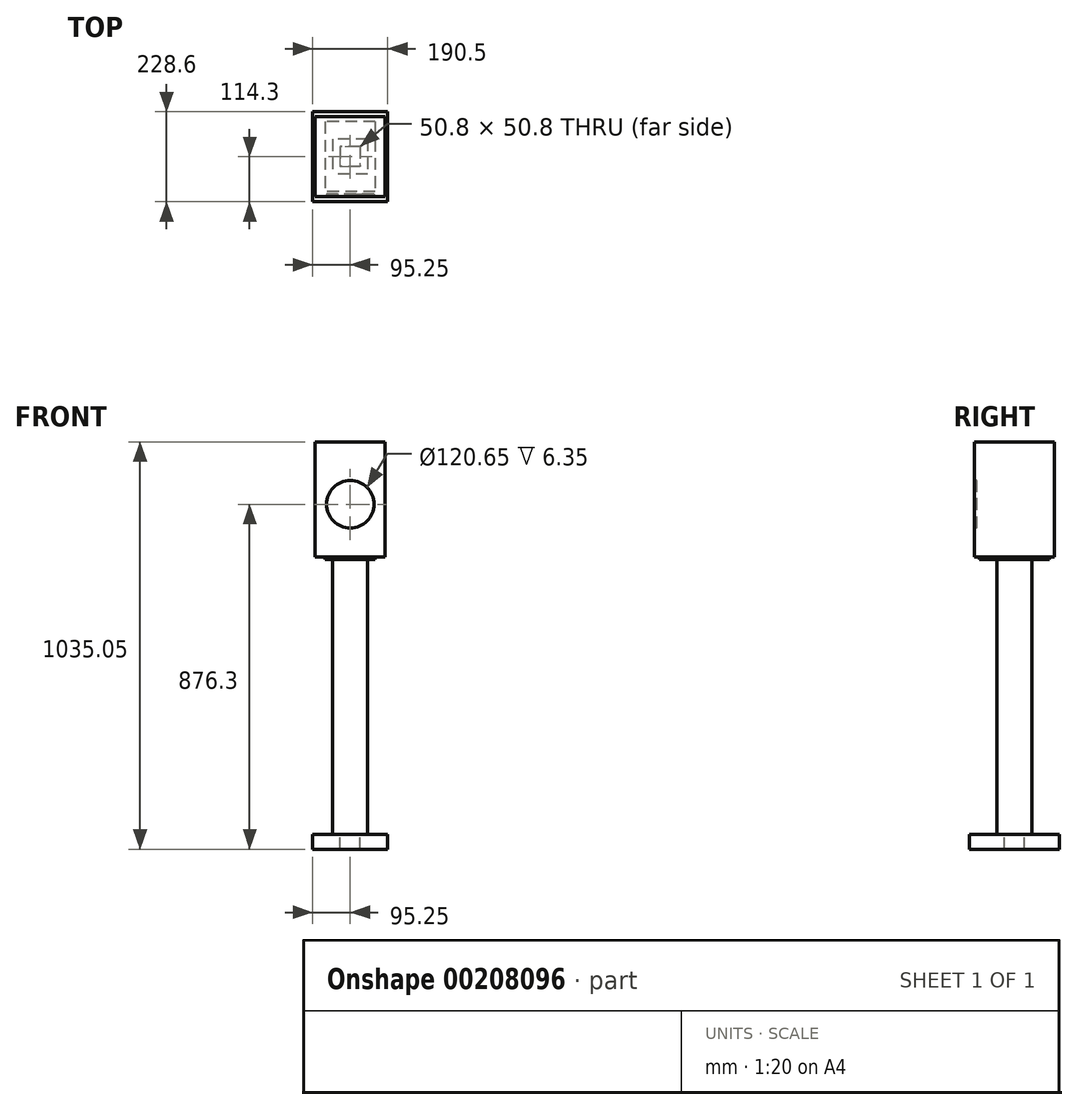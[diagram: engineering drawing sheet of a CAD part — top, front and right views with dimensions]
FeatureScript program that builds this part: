
annotation { "Feature Type Name" : "Feature", "Feature Type Description" : "" }
export const myFeature = defineFeature(function(context is Context, id is Id, definition is map)
    precondition{}
    {
        {
            var Q0;
            Q0=qCreatedBy(makeId("Top.planeOp"),FACE);
            var sketch = newSketch(context, id + "F0", { "sketchPlane" : qUnion([Q0])});
            skLineSegment(sketch, "E0.bottom", {"start": v(88.9, -101.6) * mm, "end": v(-88.9, -101.6) * mm});
            skLineSegment(sketch, "E0.top", {"start": v(88.9, 101.6) * mm, "end": v(-88.9, 101.6) * mm});
            skLineSegment(sketch, "E0.left", {"start": v(88.9, -101.6) * mm, "end": v(88.9, 101.6) * mm});
            skLineSegment(sketch, "E0.right", {"start": v(-88.9, -101.6) * mm, "end": v(-88.9, 101.6) * mm});
            skPoint(sketch, "E0.middle", {"position": v(0, 0) * mm});
            skSolve(sketch);
        }
        {
            var Q0;
            Q0 = qSketchRegion(id + "F0", true);
            extrude(context, id + "F1", {"entities" : qUnion([Q0]), "depth" : 292.1 * mm});
        }
        {
            var Q0;
            Q0=makeQuery(id+"F1.opExtrude","SWEPT_FACE",FACE,{"disambiguationData":[OSD([sQuery(id+"F0.wireOp",EDGE,"E0.bottom")])]});
            var sketch = newSketch(context, id + "F6", { "sketchPlane" : qUnion([Q0])});
            skLineSegment(sketch, "E1", {"start": v(0, 292.1) * mm, "end": v(0, 0) * mm, "construction": true});
            skCircle(sketch, "E2", {"center": v(0, 133.35) * mm, "radius": 60.33 * mm});
            skSolve(sketch);
        }
        {
            var Q0;
            Q0 = qSketchRegion(id + "F6", true);
            extrude(context, id + "F2", {"entities" : qUnion([Q0]), "operationType" : NewBodyOperationType.REMOVE, "oppositeDirection" : true, "depth" : 6.35 * mm});
        }
        {
            var Q0;
            Q0=makeQuery(id+"F1.opExtrude","CAP_FACE",FACE,{"disambiguationData":[OSD([sQuery(id+"F0.wireOp",EDGE,"E0.bottom"),sQuery(id+"F0.wireOp",EDGE,"E0.top"),sQuery(id+"F0.wireOp",EDGE,"E0.left"),sQuery(id+"F0.wireOp",EDGE,"E0.right")])],"isStart":true});
            var sketch = newSketch(context, id + "F3", { "sketchPlane" : qUnion([Q0])});
            skLineSegment(sketch, "E3", {"start": v(0, 101.6) * mm, "end": v(0, -101.6) * mm, "construction": true});
            skLineSegment(sketch, "E4", {"start": v(88.9, 0) * mm, "end": v(-88.9, 0) * mm, "construction": true});
            skLineSegment(sketch, "E5.bottom", {"start": v(63.5, -88.9) * mm, "end": v(-63.5, -88.9) * mm});
            skLineSegment(sketch, "E5.top", {"start": v(63.5, 88.9) * mm, "end": v(-63.5, 88.9) * mm});
            skLineSegment(sketch, "E5.left", {"start": v(63.5, -88.9) * mm, "end": v(63.5, 88.9) * mm});
            skLineSegment(sketch, "E5.right", {"start": v(-63.5, -88.9) * mm, "end": v(-63.5, 88.9) * mm});
            skPoint(sketch, "E5.middle", {"position": v(0, 0) * mm});
            skSolve(sketch);
        }
        {
            var Q0;
            Q0=makeQuery(id+"F3.imprint","IMPRINT",FACE,{"disambiguationData":[TD([[makeQuery(id+"F3.imprint","IMPRINT",EDGE,{"derivedFrom":sQuery(id+"F3.wireOp",EDGE,"E5.bottom")}),-1.0]])]});
            var Q1;
            Q1=sQuery(id+"F3.wireOp",EDGE,"E5.left");
            var Q2;
            Q2=sQuery(id+"F3.wireOp",EDGE,"E5.top");
            var Q3;
            Q3=sQuery(id+"F3.wireOp",EDGE,"E5.right");
            extrude(context, id + "F7", {"entities" : qUnion([Q0]), "surfaceEntities" : qUnion([Q1, Q2, Q3]), "depth" : 6.35 * mm});
        }
        {
            var Q0;
            Q0=makeQuery(id+"F7.opExtrude","CAP_FACE",FACE,{"disambiguationData":[OSD([sQuery(id+"F3.wireOp",EDGE,"E5.bottom"),sQuery(id+"F3.wireOp",EDGE,"E5.top"),sQuery(id+"F3.wireOp",EDGE,"E5.left"),sQuery(id+"F3.wireOp",EDGE,"E5.right")])],"isStart":false});
            var sketch = newSketch(context, id + "F8", { "sketchPlane" : qUnion([Q0])});
            skLineSegment(sketch, "E6.bottom", {"start": v(44.45, -44.45) * mm, "end": v(-44.45, -44.45) * mm});
            skLineSegment(sketch, "E6.top", {"start": v(44.45, 44.45) * mm, "end": v(-44.45, 44.45) * mm});
            skLineSegment(sketch, "E6.left", {"start": v(44.45, -44.45) * mm, "end": v(44.45, 44.45) * mm});
            skLineSegment(sketch, "E6.right", {"start": v(-44.45, -44.45) * mm, "end": v(-44.45, 44.45) * mm});
            skPoint(sketch, "E6.middle", {"position": v(0, 0) * mm});
            skSolve(sketch);
        }
        {
            var Q0;
            Q0 = qSketchRegion(id + "F8", true);
            extrude(context, id + "F9", {"entities" : qUnion([Q0]), "depth" : 698.5 * mm});
        }
        {
            var Q0;
            Q0=makeQuery(id+"F9.opExtrude","CAP_FACE",FACE,{"disambiguationData":[OSD([sQuery(id+"F8.wireOp",EDGE,"E6.bottom"),sQuery(id+"F8.wireOp",EDGE,"E6.top"),sQuery(id+"F8.wireOp",EDGE,"E6.left"),sQuery(id+"F8.wireOp",EDGE,"E6.right")])],"isStart":false});
            var sketch = newSketch(context, id + "F4", { "sketchPlane" : qUnion([Q0])});
            skLineSegment(sketch, "E7.bottom", {"start": v(25.4, -25.4) * mm, "end": v(-25.4, -25.4) * mm});
            skLineSegment(sketch, "E7.top", {"start": v(25.4, 25.4) * mm, "end": v(-25.4, 25.4) * mm});
            skLineSegment(sketch, "E7.left", {"start": v(25.4, -25.4) * mm, "end": v(25.4, 25.4) * mm});
            skLineSegment(sketch, "E7.right", {"start": v(-25.4, -25.4) * mm, "end": v(-25.4, 25.4) * mm});
            skPoint(sketch, "E7.middle", {"position": v(0, 0) * mm});
            skSolve(sketch);
        }
        {
            var Q0;
            Q0 = qSketchRegion(id + "F4", true);
            extrude(context, id + "F10", {"entities" : qUnion([Q0]), "operationType" : NewBodyOperationType.ADD, "depth" : 38.1 * mm});
        }
        {
            var Q0;
            Q0=makeQuery(id+"F9.opExtrude","CAP_FACE",FACE,{"disambiguationData":[OSD([sQuery(id+"F8.wireOp",EDGE,"E6.bottom"),sQuery(id+"F8.wireOp",EDGE,"E6.top"),sQuery(id+"F8.wireOp",EDGE,"E6.left"),sQuery(id+"F8.wireOp",EDGE,"E6.right")])],"isStart":false});
            var sketch = newSketch(context, id + "F5", { "sketchPlane" : qUnion([Q0])});
            skLineSegment(sketch, "E8.bottom", {"start": v(95.25, -114.3) * mm, "end": v(-95.25, -114.3) * mm});
            skLineSegment(sketch, "E8.top", {"start": v(95.25, 114.3) * mm, "end": v(-95.25, 114.3) * mm});
            skLineSegment(sketch, "E8.left", {"start": v(95.25, -114.3) * mm, "end": v(95.25, 114.3) * mm});
            skLineSegment(sketch, "E8.right", {"start": v(-95.25, -114.3) * mm, "end": v(-95.25, 114.3) * mm});
            skPoint(sketch, "E8.middle", {"position": v(0, 0) * mm});
            skLineSegment(sketch, "E9.0", {"start": v(25.4, 25.4) * mm, "end": v(-25.4, 25.4) * mm});
            skLineSegment(sketch, "E9.1", {"start": v(25.4, -25.4) * mm, "end": v(25.4, 25.4) * mm});
            skLineSegment(sketch, "E9.2", {"start": v(25.4, -25.4) * mm, "end": v(-25.4, -25.4) * mm});
            skLineSegment(sketch, "E9.3", {"start": v(-25.4, -25.4) * mm, "end": v(-25.4, 25.4) * mm});
            skSolve(sketch);
        }
        {
            var Q0;
            Q0=makeQuery(id+"F5.imprint","IMPRINT",FACE,{"disambiguationData":[TD([[makeQuery(id+"F5.imprint","IMPRINT",EDGE,{"derivedFrom":sQuery(id+"F5.wireOp",EDGE,"E8.bottom")}),-1.0]])]});
            var Q1;
            Q1=makeQuery(id+"F5.imprint","IMPRINT",FACE,{"disambiguationData":[TD([[makeQuery(id+"F5.imprint","IMPRINT",EDGE,{"derivedFrom":sQuery(id+"F5.wireOp",EDGE,"E9.0")}),-1.0]])]});
            var Q2;
            Q2=makeQuery(id+"F10.opExtrude","CAP_FACE",FACE,{"disambiguationData":[OSD([sQuery(id+"F4.wireOp",EDGE,"E7.bottom"),sQuery(id+"F4.wireOp",EDGE,"E7.top"),sQuery(id+"F4.wireOp",EDGE,"E7.left"),sQuery(id+"F4.wireOp",EDGE,"E7.right")])],"isStart":false});
            extrude(context, id + "F11", {"entities" : qUnion([Q0, Q1]), "endBound" : BoundingType.UP_TO_SURFACE, "endBoundEntityFace" : qUnion([Q2]), "depth" : 25.4 * mm});
        }
    });
